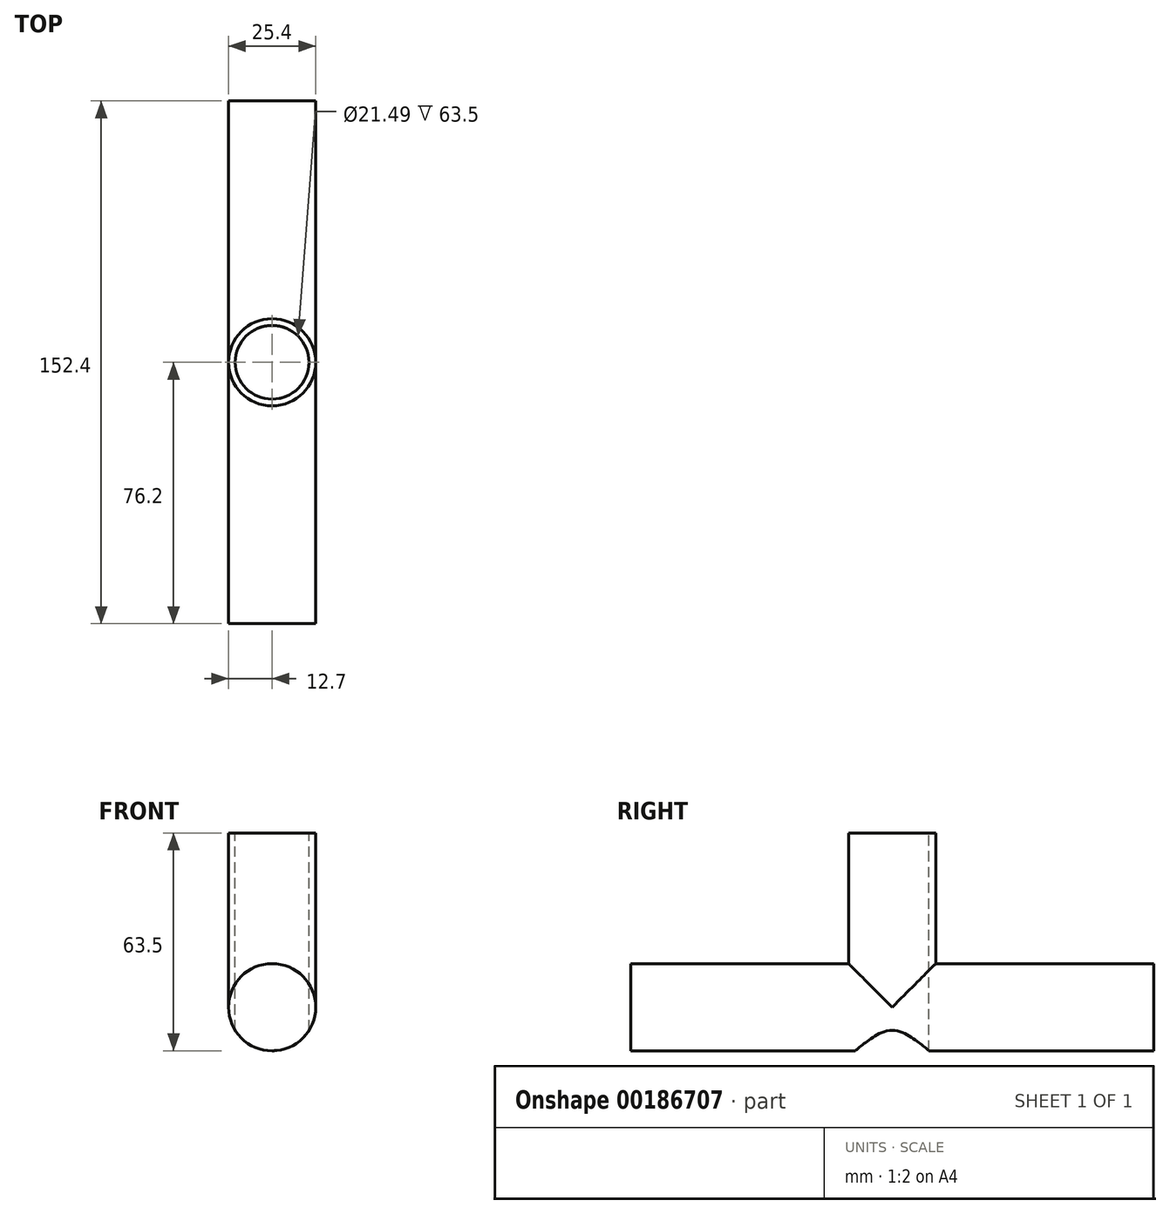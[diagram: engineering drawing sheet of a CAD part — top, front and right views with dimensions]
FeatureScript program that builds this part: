
annotation { "Feature Type Name" : "Feature", "Feature Type Description" : "" }
export const myFeature = defineFeature(function(context is Context, id is Id, definition is map)
    precondition{}
    {
        {
            var Q0;
            Q0=qCreatedBy(makeId("Front.planeOp"),FACE);
            var sketch = newSketch(context, id + "F0", { "sketchPlane" : qUnion([Q0])});
            skCircle(sketch, "E0", {"center": v(0, 0) * mm, "radius": 12.7 * mm});
            skSolve(sketch);
        }
        {
            var Q0;
            Q0=makeQuery(id+"F0.imprint","IMPRINT",FACE,{"disambiguationData":[TD([[makeQuery(id+"F0.imprint","IMPRINT",EDGE,{"derivedFrom":sQuery(id+"F0.wireOp",EDGE,"E0")}),1.0]])]});
            var Q1;
            Q1=sQuery(id+"F0.wireOp",EDGE,"E0");
            extrude(context, id + "F1", {"entities" : qUnion([Q0]), "surfaceEntities" : qUnion([Q1]), "endBound" : BoundingType.SYMMETRIC, "depth" : 152.4 * mm});
        }
        {
            var Q0;
            Q0=qCreatedBy(makeId("Top.planeOp"),FACE);
            var sketch = newSketch(context, id + "F2", { "sketchPlane" : qUnion([Q0])});
            skCircle(sketch, "E1", {"center": v(0, 0) * mm, "radius": 12.7 * mm});
            skSolve(sketch);
        }
        {
            var Q0;
            Q0 = qSketchRegion(id + "F2", true);
            extrude(context, id + "F3", {"entities" : qUnion([Q0]), "operationType" : NewBodyOperationType.ADD, "depth" : 50.8 * mm});
        }
        {
            var Q0;
            Q0=makeQuery(id+"F3.opExtrude","CAP_FACE",FACE,{"disambiguationData":[OSD([sQuery(id+"F2.wireOp",EDGE,"E1")])],"isStart":false});
            var sketch = newSketch(context, id + "F4", { "sketchPlane" : qUnion([Q0])});
            skCircle(sketch, "E2", {"center": v(0, 0) * mm, "radius": 10.75 * mm});
            skSolve(sketch);
        }
        {
            var Q0;
            Q0=makeQuery(id+"F4.imprint","IMPRINT",FACE,{"disambiguationData":[TD([[makeQuery(id+"F4.imprint","IMPRINT",EDGE,{"derivedFrom":sQuery(id+"F4.wireOp",EDGE,"E2")}),1.0]])]});
            var Q1;
            Q1=sQuery(id+"F4.wireOp",EDGE,"E2");
            extrude(context, id + "F5", {"entities" : qUnion([Q0]), "operationType" : NewBodyOperationType.REMOVE, "surfaceEntities" : qUnion([Q1]), "endBound" : BoundingType.THROUGH_ALL, "oppositeDirection" : true, "depth" : 254 * mm});
        }
    });
